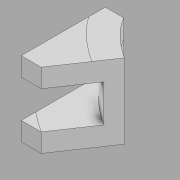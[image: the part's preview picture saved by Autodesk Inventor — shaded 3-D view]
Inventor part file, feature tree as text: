
AUTODESK INVENTOR PART (.ipt)
format: ipt  version: 2022.2 (Build 262287010, 287A)  size: 141,312 bytes
history: native  units: in
note: dims shown in document units (in); Inventor stores cm internally (conversion verified against a paired STEP export)
features: other x1, extrude x1, sketch x1, projected_geometry x1
ambient origin geometry x8: Origin, YZ Plane, XZ Plane, XY Plane, X Axis, Y Axis, Z Axis, Center Point
bodies: Solid1 (feature_tree)
feature tree (4):
  other  "Front (4)"
  extrude  "Extrusion1"  [1 undecoded]
  sketch  "Sketch1"  dims[d0=1.0in d1=0.0in]
  projected_geometry  "Projected Loop1"
note: 1 required parameter value undecoded (feature->parameter linkage not recoverable at this tier; creation-order binding heuristic only, values carry confidence <= 0.55)
